# Revit family: DS_MXT_CA_Ridgeland_Rev.0
name_source: partatom
category: Furniture
revit_build: Autodesk Revit 2016 (Build: 20150714_1515(x64)
units: mm (PartAtom-declared; Revit-internal decimal feet)

## family parameters
Always vertical = Yes
Cut with Voids When Loaded = No
OmniClass Number = 23.40.20.00
OmniClass Title = General Furniture and Specialties
Room Calculation Point = No
Shared = No
Work Plane-Based = No

## types (3) — shared parameters
2 over 2 = No
3 over 3 = No
3 over 3 Apt-Size = No
Arm Height = 28 1/2"
Assembly Code = E2020200
BIMobject Category = Furniture - Sofas & Armchairs
Body Material = Fabric
Cushion Material = Fabric
Fabric Yardage = Contact Maxwell Thomas
Fire Rating = CA117-2013
IFC Classification = Furniture
Includes Pillows = No
Leg Height = 13 1/2"
Leg Material = Leg Material
Manufacturer = Maxwell Thomas by Direct Supply
Manufacturer Contry = USA
Masterformat 2016 Code = 12 52 19
Masterformat 2016 Description = Upholstered Seating
OmniClass Code = 23-21 23 00
OmniClass Description = Residential Furniture and Equipment
Overall Depth = 32"
Overall Height = 36"
Overall Width = 31"
Product Capacity = 350lbs (159kg)
Product Collection = Ridgeland
Product Description = Upholstered Seating
Product Name = Ridgeland Tub Chair
Product Weight = 57lbs (26kg)
Seat Depth = 22"
Seat Height = 20"
Seat Width = 19 1/2"
Type Image = <None>
URL - Manufacturer = https://www.maxwellthomas.com
URL - Product = https://www.maxwellthomas.com
Uniclass 1.4 Code = L8211
Uniclass 1.4 Description = Furniture
Uniclass 2.0 Code = Pr_40_50
Uniclass 2.0 Description = Furnishings
Uniclass 2015 Code = Pr_40_50_12
Uniclass 2015 Description = Chairs, Seats and Benches
Uniformat II Code = E2020
Uniformat II Description = Movable Furnishings
Warranty Info = 5-Year Limited

## per-type parameters (varying)
| type | Ottoman | Ottoman Face | Product Number | Table/Cup Holder |
| Tub Chair | No | Yes | 0-F6405 | No |
| Tub Chair w/ Ottoman | Yes | No | 0-G6235 | No |
| Tub Chair w/ Tablet Arm | No | Yes | 0-F6421 | Yes |

## geometry (parser evidence)
native form markers: Blend x4, Sweep x2
no freeform markers — native parametric forms only
